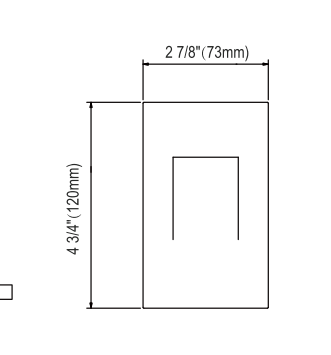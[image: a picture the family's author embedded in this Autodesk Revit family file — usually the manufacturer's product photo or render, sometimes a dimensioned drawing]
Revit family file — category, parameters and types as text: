
# Revit family: VERTICAL MINI LED STEP LIGHT
name_source: partatom
category: Lighting Fixtures
units: mm (PartAtom-declared; Revit-internal decimal feet)

## family parameters
Cut with Voids When Loaded = No
Host = Face
Light Source = Yes
Part Type = Normal
Room Calculation Point = No
Round Connector Dimension = Use Diameter
Shared = No

## types (1)
- VMSL03304-BK
    Apparent Load = 4 VA
    Average life based on 104F(HRS) = 17500
    CRI = 80
    Color Filter = 16777215
    Default Elevation = 4' - 0"
    Description = 3W LED step/wall lights are available in a vertical configuration for mounting into a Junction box. 
For poured concrete and masonry installations.For indoor and protected outdoor use.
    Dimming Lamp Color Temperature Shift = <None>
    Finish/Color = ALUMINUM BLACK
    Fixture Height = 0' - 1 1/2"
    Fixture Length = 0' - 2 7/8"
    Fixture Width = 0' - 4 3/4"
    GLASS = Glass
    IP Rating = Wet Location
    Lamp = LED
    Manufacturer = Above All Lighting
    Model = VMSL03304-BK
    Order number = 15667
    Photometric Web File = VMSL03304-BK_IESNA2002.IES
    Tilt Angle = 180.00°
    Type Comments = VERTICAL MINI LED STEP LIGHT
    URL = https://www.abovealllighting.com
    Voltage = 120 V
    WATTS = 3 W

## geometry (parser evidence)
native form markers: Sweep x8
no freeform markers — native parametric forms only
